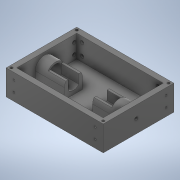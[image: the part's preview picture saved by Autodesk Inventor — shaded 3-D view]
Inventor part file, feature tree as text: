
AUTODESK INVENTOR PART (.ipt)
format: ipt  version: 2020 (Build 240168000, 168)  size: 543,744 bytes
history: native  units: in
note: dims shown in document units (in); Inventor stores cm internally (conversion verified against a paired STEP export)
features: projected_geometry x15, extrude x12, sketch x11, mirror x3
ambient origin geometry x8: Origin, YZ Plane, XZ Plane, XY Plane, X Axis, Y Axis, Z Axis, Center Point
bodies: Solid1 (feature_tree)
feature tree (41):
  extrude  "Extrusion1"  Depth=3.1496in
  extrude  "Extrusion2"  Depth=1.0005in TaperAngle=0.0deg
  extrude  "Extrusion5"  Depth=0.0787in
  extrude  "Extrusion6"  Depth=0.7874in TaperAngle=0.0deg
  extrude  "Extrusion7"  Depth=3.8583in
  mirror  "Mirror2"
  extrude  "Extrusion24"  Depth=2.6772in
  extrude  "Extrusion25"  Depth=0.1575in
  extrude  "Extrusion26"  Depth=0.0866in
  mirror  "Mirror11"
  extrude  "Extrusion27"  Depth=0.0866in
  extrude  "Extrusion28"  Depth=0.0866in
  extrude  "Extrusion29"  Depth=0.0866in TaperAngle=0.0deg
  extrude  "Extrusion30"  Depth=0.2362in
  mirror  "Mirror13"
  sketch  "Sketch1"  dims[d0=4.3307in d1=3.1496in]
  sketch  "Sketch2"  dims[d2=0.1181in d3=0.0in d5=1.0005in d6=0.0in]
  projected_geometry  "Projected Loop1"
  sketch  "Sketch8"  dims[d18=0.5906in d20=0.0787in]
  projected_geometry  "Projected Loop5"
  sketch  "Sketch9"  dims[d21=0.5118in d22=0.0in d25=0.7874in d26=0.0in]
  sketch  "Sketch28"  dims[d30=0.4626in d31=0.0in d36=3.8583in]
  projected_geometry  "Projected Loop15"
  sketch  "Sketch29"  dims[d37=2.6772in d120=0.1575in]
  projected_geometry  "Projected Loop16"
  projected_geometry  "Projected Loop17"
  projected_geometry  "Projected Loop18"
  projected_geometry  "Projected Loop19"
  sketch  "Sketch30"  dims[d121=0.1575in d122=0.1575in]
  projected_geometry  "Projected Loop20"
  projected_geometry  "Projected Loop21"
  sketch  "Sketch31"  dims[d123=0.1575in d124=0.0866in]
  projected_geometry  "Projected Loop22"
  sketch  "Sketch32"  dims[d125=0.0in d126=0.0866in]
  projected_geometry  "Projected Loop23"
  projected_geometry  "Projected Loop24"
  sketch  "Sketch33"  dims[d127=0.0866in d128=0.0866in]
  projected_geometry  "Projected Loop25"
  sketch  "Sketch34"  dims[d129=0.0866in d130=2.2126in d131=0.0in d132=0.2362in d133=0.2362in d134=0.2362in d135=0.1181in d136=0.1181in d137=0.1142in d138=0.1181in d139=0.1142in d140=0.2756in d141=0.0in d144=1.4665in d145=0.6102in d146=0.6102in d147=0.4803in d148=0.1378in d150=0.1181in d152=0.1575in d153=0.2918in d154=0.1575in d155=0.2362in d156=0.0866in d157=0.0in d158=0.0866in d159=0.0866in d160=0.0866in d161=0.0in d162=0.1181in d163=0.1575in d164=0.1575in d165=0.2918in d166=0.2362in d167=0.0866in d168=0.0in d169=0.0866in d170=0.0866in d171=0.0866in d172=0.0in d50=0.0197in d51=0.0344in d52=0.0197in d53=0.0344in d73=0.0197in d74=0.0344in d75=0.0197in d76=0.0344in]
  projected_geometry  "Projected Loop26"
  projected_geometry  "Projected Loop27"
